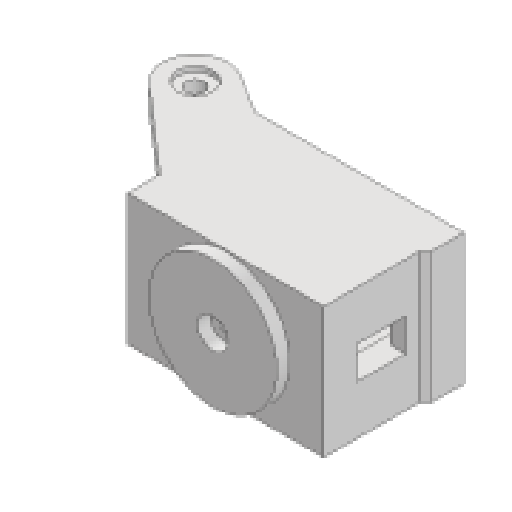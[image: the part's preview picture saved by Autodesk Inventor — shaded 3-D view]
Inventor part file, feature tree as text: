
AUTODESK INVENTOR PART (.ipt)
format: ipt  version: 2025 (Build 290162010, 162A)  size: 258,560 bytes
history: native  units: in
note: dims shown in document units (in); Inventor stores cm internally (conversion verified against a paired STEP export)
features: extrude x11, sketch x10, plane x2, mirror x2, chamfer x1, projected_geometry x1
ambient origin geometry x8: Origin, YZ Plane, XZ Plane, XY Plane, X Axis, Y Axis, Z Axis, Center Point
bodies: Solid1 (feature_tree)
feature tree (27):
  extrude  "Extrusion1"  Depth=0.5in
  extrude  "Extrusion2"  Depth=0.618in TaperAngle=0.0deg
  extrude  "Extrusion3"  Depth=0.3in
  chamfer  "Chamfer1"  Distance=0.618in
  extrude  "Extrusion4"  Depth=0.2in TaperAngle=0.0deg
  plane  "Work Plane1"
  extrude  "Extrusion5"  Depth=0.037in
  plane  "Work Plane2"
  mirror  "Mirror1"
  extrude  "Extrusion6"  Depth=0.187in
  mirror  "Mirror2"
  extrude  "Extrusion9"  Depth=0.2in
  extrude  "Extrusion10"  Depth=0.11in
  sketch  "Sketch11"  dims[d27=0.55in d29=0.22in]
  extrude  "Extrusion11"  Depth=0.22in
  extrude  "Extrusion12"  Depth=0.2in
  extrude  "Extrusion13"  Depth=0.055in
  sketch  "Sketch1"  dims[d0=0.9in d1=0.5in]
  sketch  "Sketch2"  dims[d2=0.8in d3=0.618in d4=0.0in]
  sketch  "Sketch3"  dims[d5=0.2in d6=0.3in d7=0.618in d8=0.0in]
  sketch  "Sketch4"  dims[d9=0.187in d10=0.2in d11=0.0in]
  sketch  "Sketch5"  dims[d12=0.037in d13=0.125in d14=45.0deg d15=0.07in]
  sketch  "Sketch6"  dims[d16=0.3in d17=0.0in d18=0.187in]
  sketch  "Sketch9"  dims[d21=0.15in d22=0.0in d24=0.2in]
  sketch  "Sketch10"  dims[d25=0.35in d26=0.11in]
  projected_geometry  "Projected Loop2"
  sketch  "Sketch12"  dims[d30=0.03in d31=0.0in d37=0.2in d38=0.055in d39=0.1in d40=0.875in d41=0.0in d42=0.6in d43=0.2in d44=0.0in d45=0.08in d46=0.184in d47=0.3in d48=0.08in d49=0.0in d50=0.3375in d51=0.0in d52=0.17in d53=0.09in d54=0.0in]
